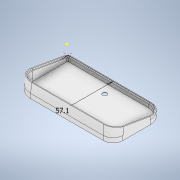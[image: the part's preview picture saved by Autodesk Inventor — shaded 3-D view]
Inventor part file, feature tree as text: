
AUTODESK INVENTOR PART (.ipt)
format: ipt  version: 2020 (Build 240168000, 168)  size: 555,520 bytes
history: native  units: in
note: dims shown in document units (in); Inventor stores cm internally (conversion verified against a paired STEP export)
features: sketch x7, extrude x4, projected_geometry x4, revolve x2
ambient origin geometry x8: Origin, YZ Plane, XZ Plane, XY Plane, X Axis, Y Axis, Z Axis, Center Point
bodies: Body1 (feature_tree)
feature tree (17):
  sketch  "Sketch1"  dims[d0=2.248in d10=0.0687in]
  revolve  "Revolution1"  [1 undecoded]
  extrude  "Extrusion4"  Depth=0.0394in
  extrude  "Extrusion5"  Depth=0.0394in
  revolve  "Revolution2"  [1 undecoded]
  extrude  "Extrusion6"  Depth=2.0866in
  extrude  "Extrusion8"  Depth=0.0787in TaperAngle=0.0deg
  sketch  "Sketch3"  dims[d11=0.1969in d12=0.0in d13=0.0394in]
  sketch  "Sketch8"  dims[d14=0.0591in d15=0.0in d16=0.0394in]
  projected_geometry  "Projected Loop4"
  sketch  "Sketch9"  dims[d17=0.0687in d18=0.1378in d19=0.0in]
  projected_geometry  "Projected Loop5"
  sketch  "Sketch10"  dims[d23=0.1969in d24=2.0866in]
  projected_geometry  "Projected Loop6"
  sketch  "Sketch11"  dims[d25=0.4921in d26=0.0787in d27=0.0in]
  projected_geometry  "Projected Loop7"
  sketch  "Sketch14"  dims[d1=0.0344in d2=0.0344in d7=0.0197in d8=0.0344in d9=0.0197in]
note: 2 required parameter values undecoded (feature->parameter linkage not recoverable at this tier; creation-order binding heuristic only, values carry confidence <= 0.55)
